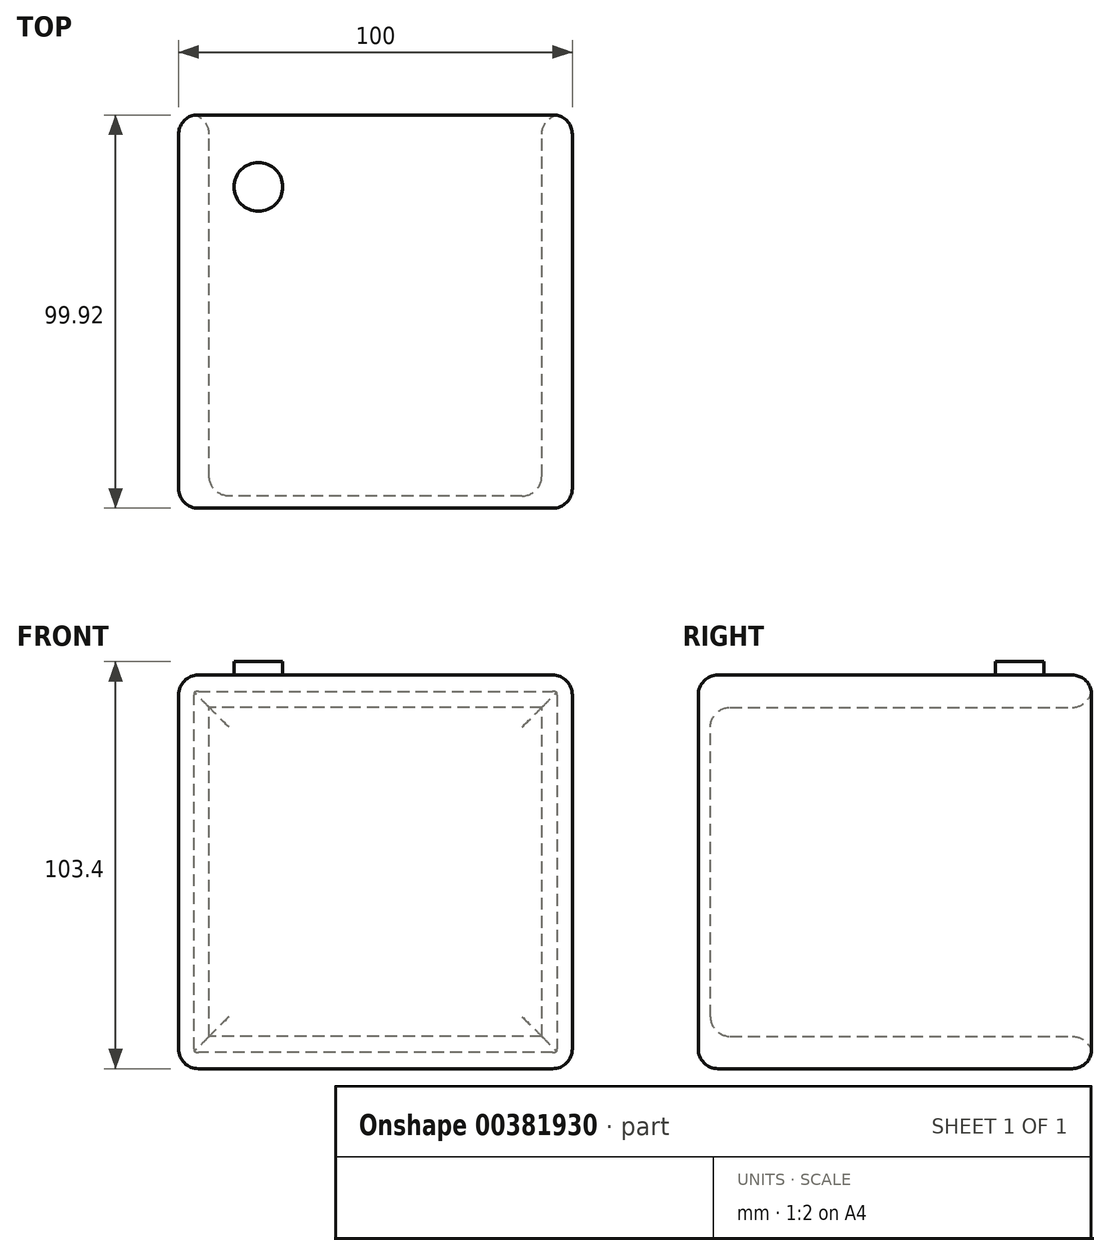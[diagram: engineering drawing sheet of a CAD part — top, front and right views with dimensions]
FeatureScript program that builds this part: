
annotation { "Feature Type Name" : "Feature", "Feature Type Description" : "" }
export const myFeature = defineFeature(function(context is Context, id is Id, definition is map)
    precondition{}
    {
        {
            var Q0;
            Q0=qCreatedBy(makeId("Front.planeOp"),FACE);
            var sketch = newSketch(context, id + "F0", { "sketchPlane" : qUnion([Q0])});
            skLineSegment(sketch, "E0.bottom", {"start": v(50, 50) * mm, "end": v(-50, 50) * mm});
            skLineSegment(sketch, "E0.top", {"start": v(50, -50) * mm, "end": v(-50, -50) * mm});
            skLineSegment(sketch, "E0.left", {"start": v(50, 50) * mm, "end": v(50, -50) * mm});
            skLineSegment(sketch, "E0.right", {"start": v(-50, 50) * mm, "end": v(-50, -50) * mm});
            skPoint(sketch, "E0.middle", {"position": v(0, 0) * mm});
            skSolve(sketch);
        }
        {
            var Q0;
            Q0 = qSketchRegion(id + "F0", true);
            extrude(context, id + "F1", {"entities" : qUnion([Q0]), "depth" : 100 * mm});
        }
        {
            var Q0;
            Q0=makeQuery(id+"F1.opExtrude","CAP_EDGE",EDGE,{"disambiguationData":[OSD([sQuery(id+"F0.wireOp",EDGE,"E0.bottom")])],"isStart":false});
            var Q1;
            Q1=makeQuery(id+"F1.opExtrude","CAP_EDGE",EDGE,{"disambiguationData":[OSD([sQuery(id+"F0.wireOp",EDGE,"E0.right")])],"isStart":false});
            var Q2;
            Q2=makeQuery(id+"F1.opExtrude","CAP_EDGE",EDGE,{"disambiguationData":[OSD([sQuery(id+"F0.wireOp",EDGE,"E0.top")])],"isStart":false});
            var Q3;
            Q3=makeQuery(id+"F1.opExtrude","CAP_EDGE",EDGE,{"disambiguationData":[OSD([sQuery(id+"F0.wireOp",EDGE,"E0.left")])],"isStart":false});
            var Q4;
            Q4=makeQuery(id+"F1.opExtrude","SWEPT_EDGE",EDGE,{"disambiguationData":[OSD([sQuery(id+"F0.wireOp",EDGE,"E0.top"),sQuery(id+"F0.wireOp",EDGE,"E0.left")])]});
            var Q5;
            Q5=makeQuery(id+"F1.opExtrude","SWEPT_FACE",FACE,{"disambiguationData":[OSD([sQuery(id+"F0.wireOp",EDGE,"E0.top")])]});
            var Q6;
            Q6=makeQuery(id+"F1.opExtrude","SWEPT_FACE",FACE,{"disambiguationData":[OSD([sQuery(id+"F0.wireOp",EDGE,"E0.bottom")])]});
            var Q7;
            Q7=makeQuery(id+"F1.opExtrude","CAP_FACE",FACE,{"disambiguationData":[OSD([sQuery(id+"F0.wireOp",EDGE,"E0.bottom"),sQuery(id+"F0.wireOp",EDGE,"E0.top"),sQuery(id+"F0.wireOp",EDGE,"E0.left"),sQuery(id+"F0.wireOp",EDGE,"E0.right")])],"isStart":true});
            fillet(context, id + "F2", {"entities" : qUnion([Q0, Q1, Q2, Q3, Q4, Q5, Q6, Q7]), "radius" : 5 * mm, "tangentPropagation" : true, "allowEdgeOverflow" : false});
        }
        {
            var Q0;
            Q0=qCreatedBy(makeId("Front.planeOp"),FACE);
            var sketch = newSketch(context, id + "F3", { "sketchPlane" : qUnion([Q0])});
            skLineSegment(sketch, "E1.bottom", {"start": v(42.24, -41.79) * mm, "end": v(-42.24, -41.79) * mm});
            skLineSegment(sketch, "E1.top", {"start": v(42.24, 41.79) * mm, "end": v(-42.24, 41.79) * mm});
            skLineSegment(sketch, "E1.left", {"start": v(42.24, -41.79) * mm, "end": v(42.24, 41.79) * mm});
            skLineSegment(sketch, "E1.right", {"start": v(-42.24, -41.79) * mm, "end": v(-42.24, 41.79) * mm});
            skPoint(sketch, "E1.middle", {"position": v(0, 0) * mm});
            skSolve(sketch);
        }
        {
            var Q0;
            Q0 = qSketchRegion(id + "F3", true);
            extrude(context, id + "F4", {"entities" : qUnion([Q0]), "operationType" : NewBodyOperationType.REMOVE, "depth" : 96.9 * mm});
        }
        {
            var Q0;
            Q0=makeQuery(id+"F4.boolean.opBoolean","COPY",FACE,{"derivedFrom":makeQuery(id+"F4.opExtrude","CAP_FACE",FACE,{"disambiguationData":[OSD([sQuery(id+"F3.wireOp",EDGE,"E1.bottom"),sQuery(id+"F3.wireOp",EDGE,"E1.top"),sQuery(id+"F3.wireOp",EDGE,"E1.left"),sQuery(id+"F3.wireOp",EDGE,"E1.right")])],"isStart":false})});
            fillet(context, id + "F5", {"entities" : qUnion([Q0]), "radius" : 5 * mm, "tangentPropagation" : true, "allowEdgeOverflow" : false});
        }
        {
            var Q0;
            Q0=makeQuery(id+"F1.opExtrude","CAP_FACE",FACE,{"disambiguationData":[OSD([sQuery(id+"F0.wireOp",EDGE,"E0.bottom"),sQuery(id+"F0.wireOp",EDGE,"E0.top"),sQuery(id+"F0.wireOp",EDGE,"E0.left"),sQuery(id+"F0.wireOp",EDGE,"E0.right")])],"isStart":true});
            fillet(context, id + "F6", {"entities" : qUnion([Q0]), "radius" : 5 * mm, "tangentPropagation" : true, "allowEdgeOverflow" : false});
        }
        {
            var Q0;
            Q0=makeQuery(id+"F1.opExtrude","SWEPT_FACE",FACE,{"disambiguationData":[OSD([sQuery(id+"F0.wireOp",EDGE,"E0.bottom")])]});
            var sketch = newSketch(context, id + "F7", { "sketchPlane" : qUnion([Q0])});
            skCircle(sketch, "E2", {"center": v(-29.74, -18.36) * mm, "radius": 6.2 * mm});
            skSolve(sketch);
        }
        {
            var Q0;
            Q0 = qSketchRegion(id + "F7", true);
            extrude(context, id + "F8", {"entities" : qUnion([Q0]), "operationType" : NewBodyOperationType.ADD, "depth" : 3.4 * mm});
        }
    });
